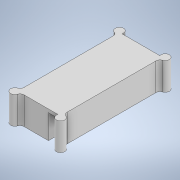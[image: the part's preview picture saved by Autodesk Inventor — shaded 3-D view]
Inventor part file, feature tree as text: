
AUTODESK INVENTOR PART (.ipt)
format: ipt  version: 2020 (Build 240168000, 168)  size: 208,384 bytes
history: native  units: in
note: dims shown in document units (in); Inventor stores cm internally (conversion verified against a paired STEP export)
features: extrude x7, sketch x7, projected_geometry x4, fillet x3, mirror x3, plane x2
ambient origin geometry x8: Origin, YZ Plane, XZ Plane, XY Plane, X Axis, Y Axis, Z Axis, Center Point
bodies: Solid1 (feature_tree)
feature tree (26):
  extrude  "Extrusion1"  Depth=2.5in
  extrude  "Extrusion2"  Depth=0.75in TaperAngle=0.0deg
  extrude  "Extrusion3"  Depth=0.1in
  extrude  "Extrusion4"  Depth=0.33in
  extrude  "Extrusion5"  Depth=0.25in
  extrude  "Extrusion6"  Depth=0.1in TaperAngle=0.0deg
  extrude  "Extrusion7"  Depth=0.125in
  fillet  "Fillet1"  Radius=0.08in
  plane  "Work Plane1"
  mirror  "Mirror1"
  plane  "Work Plane2"
  mirror  "Mirror2"
  fillet  "Fillet2"  Radius=0.13in
  mirror  "Mirror3"
  fillet  "Fillet3"  Radius=0.4in
  sketch  "Sketch1"  dims[d0=1.08in d1=2.5in]
  sketch  "Sketch2"  dims[d2=0.125in d3=0.75in d4=0.0in]
  projected_geometry  "Projected Loop1"
  sketch  "Sketch3"  dims[d5=0.1in d6=0.0in d7=0.1in]
  sketch  "Sketch4"  dims[d8=0.63in d9=0.33in]
  sketch  "Sketch5"  dims[d10=0.1in d11=0.0in d12=0.25in]
  projected_geometry  "Projected Loop2"
  sketch  "Sketch6"  dims[d13=0.1in d14=0.0in d15=0.4in d16=0.0in]
  projected_geometry  "Projected Loop3"
  sketch  "Sketch7"  dims[d17=0.1in d18=0.08in d19=0.08in d20=0.13in d21=0.4in d22=0.0in d23=0.4in d24=0.0in d25=0.125in d26=0.125in d27=0.125in]
  projected_geometry  "Projected Loop4"
